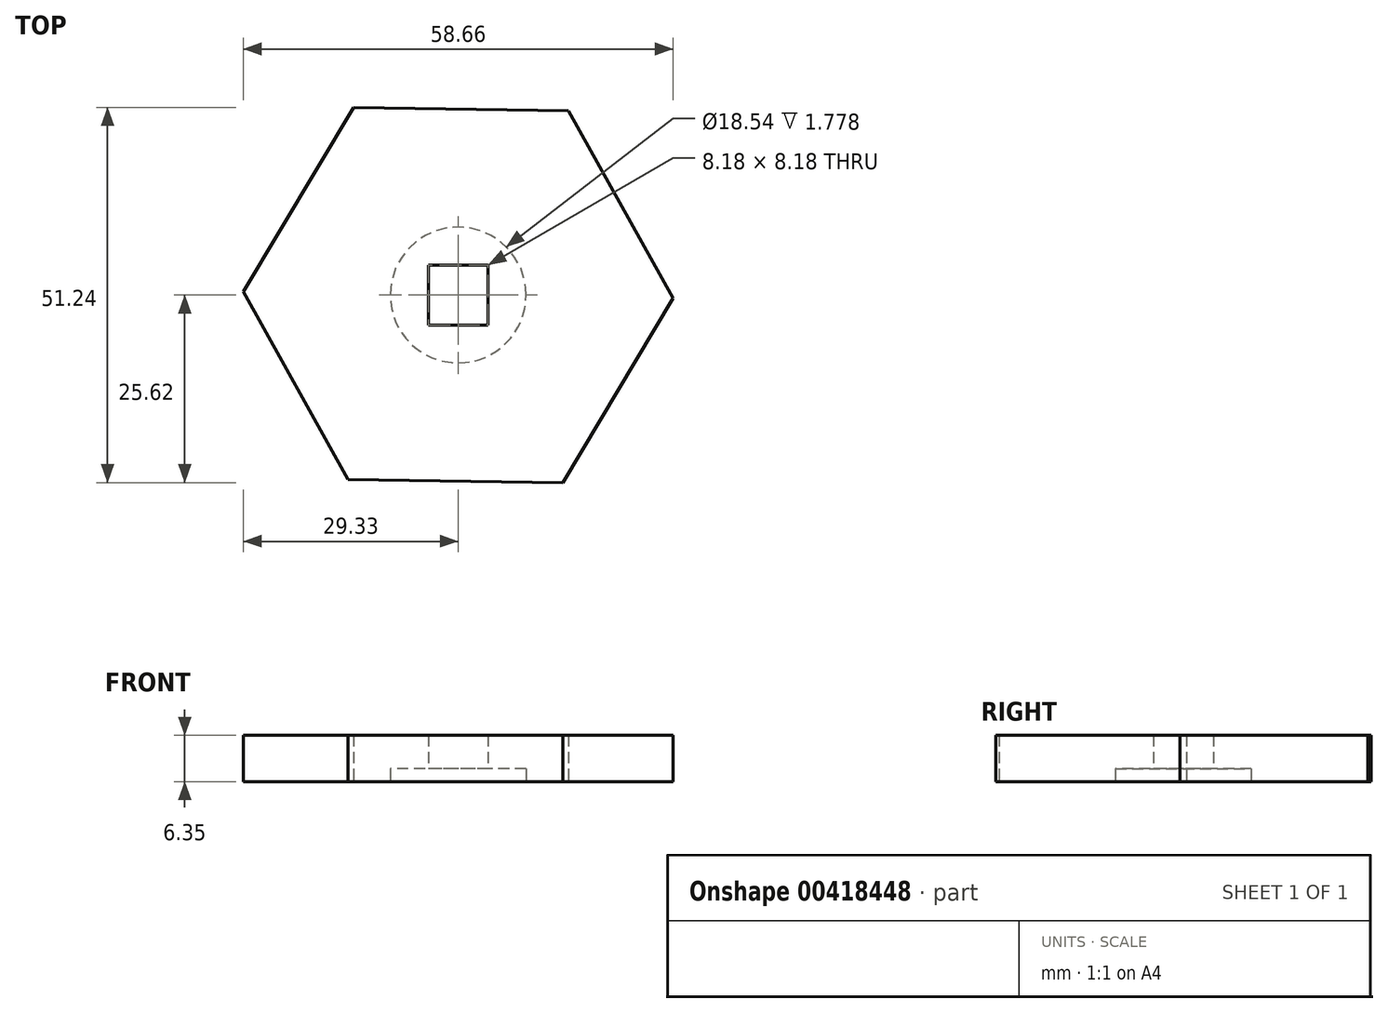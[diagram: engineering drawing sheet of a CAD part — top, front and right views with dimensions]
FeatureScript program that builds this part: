
annotation { "Feature Type Name" : "Feature", "Feature Type Description" : "" }
export const myFeature = defineFeature(function(context is Context, id is Id, definition is map)
    precondition{}
    {
        {
            var Q0;
            Q0=qCreatedBy(makeId("Top.planeOp"),FACE);
            var sketch = newSketch(context, id + "F0", { "sketchPlane" : qUnion([Q0])});
            skCircle(sketch, "E0", {"center": v(0, 0) * mm, "radius": 25.4 * mm});
            skCircle(sketch, "E1.cCircle", {"center": v(0, 0) * mm, "radius": 25.4 * mm, "construction": true});
            skLineSegment(sketch, "E1.0", {"start": v(-29.33, 0.46) * mm, "end": v(-14.27, 25.62) * mm});
            skLineSegment(sketch, "E1.1", {"start": v(-14.27, 25.62) * mm, "end": v(15.06, 25.17) * mm});
            skLineSegment(sketch, "E1.2", {"start": v(15.06, 25.17) * mm, "end": v(29.33, -0.46) * mm});
            skLineSegment(sketch, "E1.3", {"start": v(29.33, -0.46) * mm, "end": v(14.27, -25.62) * mm});
            skLineSegment(sketch, "E1.4", {"start": v(14.27, -25.62) * mm, "end": v(-15.06, -25.17) * mm});
            skLineSegment(sketch, "E1.5", {"start": v(-15.06, -25.17) * mm, "end": v(-29.33, 0.46) * mm});
            skPoint(sketch, "E1.0.midPoint", {"position": v(-21.8, 13.04) * mm});
            skLineSegment(sketch, "E2.bottom", {"start": v(4.09, 4.09) * mm, "end": v(-4.09, 4.09) * mm});
            skLineSegment(sketch, "E2.top", {"start": v(4.09, -4.09) * mm, "end": v(-4.09, -4.09) * mm});
            skLineSegment(sketch, "E2.left", {"start": v(4.09, 4.09) * mm, "end": v(4.09, -4.09) * mm});
            skLineSegment(sketch, "E2.right", {"start": v(-4.09, 4.09) * mm, "end": v(-4.09, -4.09) * mm});
            skCircle(sketch, "E3", {"center": v(0, 0) * mm, "radius": 9.27 * mm});
            skSolve(sketch);
        }
        {
            var Q0;
            {var subQ0=sQuery(id+"F0.wireOp",EDGE,"E0");var subQ4=makeQuery(id+"F0.imprint","INTERSECT",VERTEX,{"derivedFrom":[subQ0,sQuery(id+"F0.wireOp",EDGE,"E1.1")]});Q0=makeQuery(id+"F0.imprint","IMPRINT",FACE,{"disambiguationData":[TD([[makeQuery(id+"F0.imprint","IMPRINT",EDGE,{"disambiguationData":[TD([[subQ4,1.0]])],"derivedFrom":subQ0}),1.0]])]});}
            var Q1;
            {var subQ0=sQuery(id+"F0.wireOp",EDGE,"E1.1");var subQ1=sQuery(id+"F0.wireOp",EDGE,"E0");var subQ2=makeQuery(id+"F0.imprint","INTERSECT",VERTEX,{"derivedFrom":[subQ1,subQ0]});Q1=makeQuery(id+"F0.imprint","IMPRINT",FACE,{"disambiguationData":[TD([[makeQuery(id+"F0.imprint","IMPRINT",EDGE,{"disambiguationData":[TD([[subQ2,-1.0]])],"derivedFrom":subQ1}),-1.0]])]});}
            var Q2;
            {var subQ0=sQuery(id+"F0.wireOp",EDGE,"E1.1");var subQ1=sQuery(id+"F0.wireOp",EDGE,"E0");var subQ2=makeQuery(id+"F0.imprint","INTERSECT",VERTEX,{"derivedFrom":[subQ1,subQ0]});Q2=makeQuery(id+"F0.imprint","IMPRINT",FACE,{"disambiguationData":[TD([[makeQuery(id+"F0.imprint","IMPRINT",EDGE,{"disambiguationData":[TD([[subQ2,1.0]])],"derivedFrom":subQ1}),-1.0]])]});}
            var Q3;
            {var subQ0=sQuery(id+"F0.wireOp",EDGE,"E1.2");var subQ1=sQuery(id+"F0.wireOp",EDGE,"E0");var subQ2=makeQuery(id+"F0.imprint","INTERSECT",VERTEX,{"derivedFrom":[subQ1,subQ0]});Q3=makeQuery(id+"F0.imprint","IMPRINT",FACE,{"disambiguationData":[TD([[makeQuery(id+"F0.imprint","IMPRINT",EDGE,{"disambiguationData":[TD([[subQ2,1.0]])],"derivedFrom":subQ1}),-1.0]])]});}
            var Q4;
            {var subQ0=sQuery(id+"F0.wireOp",EDGE,"E1.4");var subQ1=sQuery(id+"F0.wireOp",EDGE,"E0");var subQ2=makeQuery(id+"F0.imprint","INTERSECT",VERTEX,{"derivedFrom":[subQ1,subQ0]});Q4=makeQuery(id+"F0.imprint","IMPRINT",FACE,{"disambiguationData":[TD([[makeQuery(id+"F0.imprint","IMPRINT",EDGE,{"disambiguationData":[TD([[subQ2,-1.0]])],"derivedFrom":subQ1}),-1.0]])]});}
            var Q5;
            {var subQ0=sQuery(id+"F0.wireOp",EDGE,"E1.5");var subQ1=sQuery(id+"F0.wireOp",EDGE,"E0");var subQ2=makeQuery(id+"F0.imprint","INTERSECT",VERTEX,{"derivedFrom":[subQ1,subQ0]});Q5=makeQuery(id+"F0.imprint","IMPRINT",FACE,{"disambiguationData":[TD([[makeQuery(id+"F0.imprint","IMPRINT",EDGE,{"disambiguationData":[TD([[subQ2,-1.0]])],"derivedFrom":subQ1}),-1.0]])]});}
            var Q6;
            {var subQ0=sQuery(id+"F0.wireOp",EDGE,"E1.0");var subQ1=sQuery(id+"F0.wireOp",EDGE,"E0");var subQ2=makeQuery(id+"F0.imprint","INTERSECT",VERTEX,{"derivedFrom":[subQ1,subQ0]});Q6=makeQuery(id+"F0.imprint","IMPRINT",FACE,{"disambiguationData":[TD([[makeQuery(id+"F0.imprint","IMPRINT",EDGE,{"disambiguationData":[TD([[subQ2,-1.0]])],"derivedFrom":subQ1}),-1.0]])]});}
            var Q7;
            Q7=makeQuery(id+"F0.imprint","IMPRINT",FACE,{"disambiguationData":[TD([[makeQuery(id+"F0.imprint","IMPRINT",EDGE,{"derivedFrom":sQuery(id+"F0.wireOp",EDGE,"E2.bottom")}),-1.0]])]});
            extrude(context, id + "F1", {"entities" : qUnion([Q0, Q1, Q2, Q3, Q4, Q5, Q6, Q7]), "depth" : 6.35 * mm});
        }
        {
            var Q0;
            Q0=makeQuery(id+"F0.imprint","IMPRINT",FACE,{"disambiguationData":[TD([[makeQuery(id+"F0.imprint","IMPRINT",EDGE,{"derivedFrom":sQuery(id+"F0.wireOp",EDGE,"E2.bottom")}),-1.0]])]});
            extrude(context, id + "F2", {"entities" : qUnion([Q0]), "operationType" : NewBodyOperationType.REMOVE, "depth" : 1.78 * mm});
        }
    });
